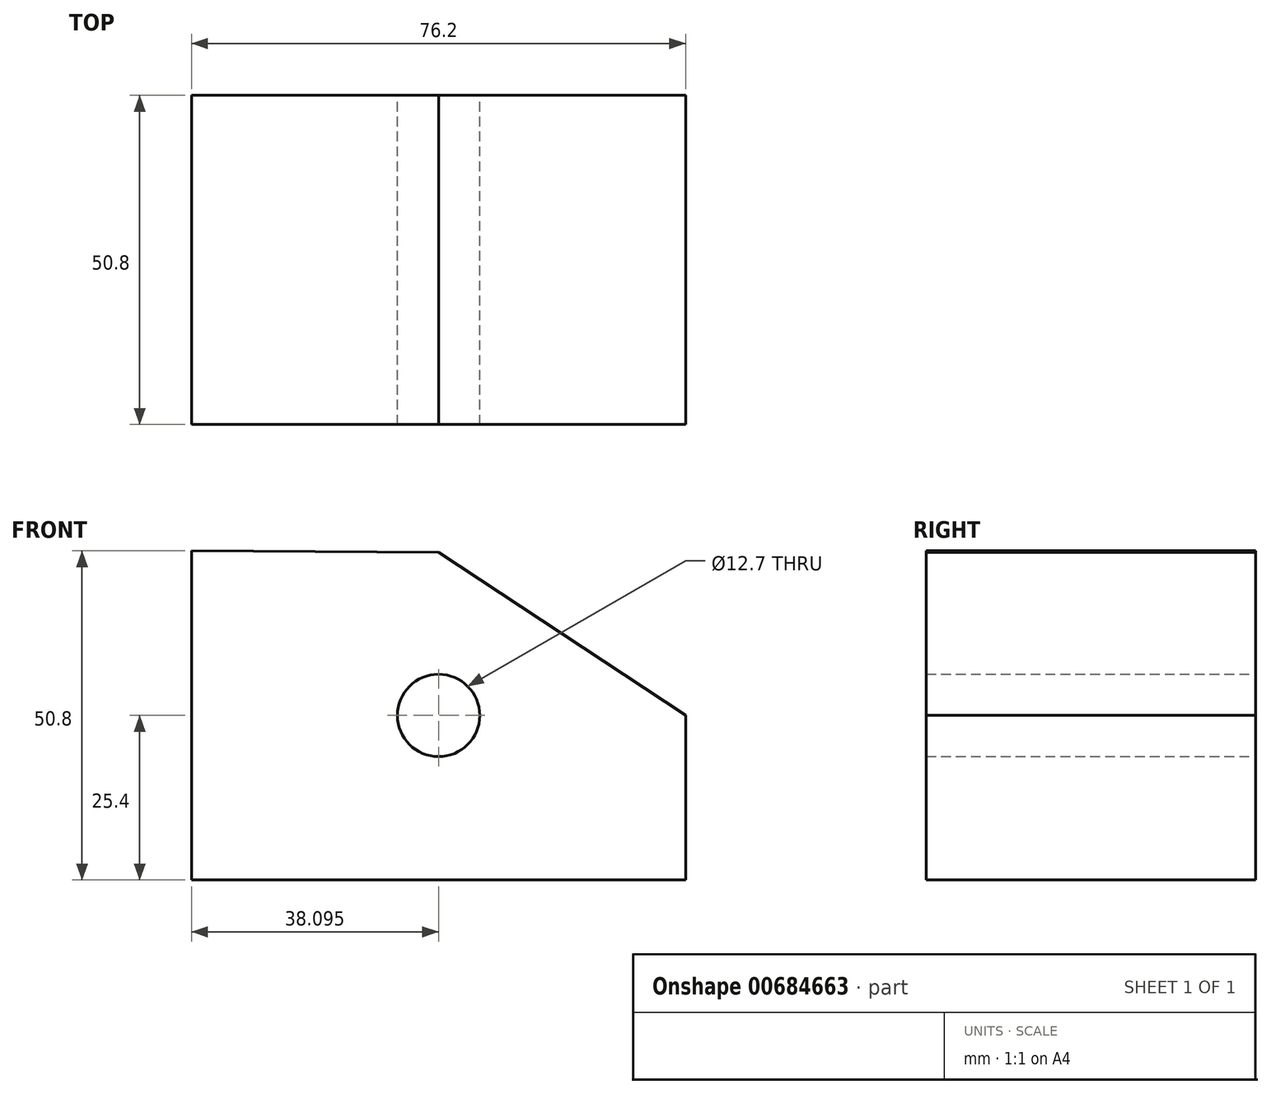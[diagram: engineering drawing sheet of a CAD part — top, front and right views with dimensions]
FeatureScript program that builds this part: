
annotation { "Feature Type Name" : "Feature", "Feature Type Description" : "" }
export const myFeature = defineFeature(function(context is Context, id is Id, definition is map)
    precondition{}
    {
        {
            var Q0;
            Q0=qCreatedBy(makeId("Front.planeOp"),FACE);
            var sketch = newSketch(context, id + "F0", { "sketchPlane" : qUnion([Q0])});
            skLineSegment(sketch, "E0", {"start": v(-33.13, 28.66) * mm, "end": v(-33.13, -22.14) * mm});
            skLineSegment(sketch, "E1", {"start": v(-33.13, -22.14) * mm, "end": v(43.07, -22.14) * mm});
            skLineSegment(sketch, "E2", {"start": v(43.07, -22.14) * mm, "end": v(43.07, 3.26) * mm});
            skLineSegment(sketch, "E3", {"start": v(43.07, 3.26) * mm, "end": v(4.97, 28.43) * mm});
            skLineSegment(sketch, "E4", {"start": v(4.97, 28.43) * mm, "end": v(-33.13, 28.66) * mm});
            skCircle(sketch, "E5", {"center": v(4.97, 3.26) * mm, "radius": 6.35 * mm});
            skSolve(sketch);
        }
        {
            var Q0;
            Q0 = qSketchRegion(id + "F0", true);
            extrude(context, id + "F1", {"entities" : qUnion([Q0]), "depth" : 50.8 * mm, "offsetDistance" : 25.4 * mm});
        }
    });
